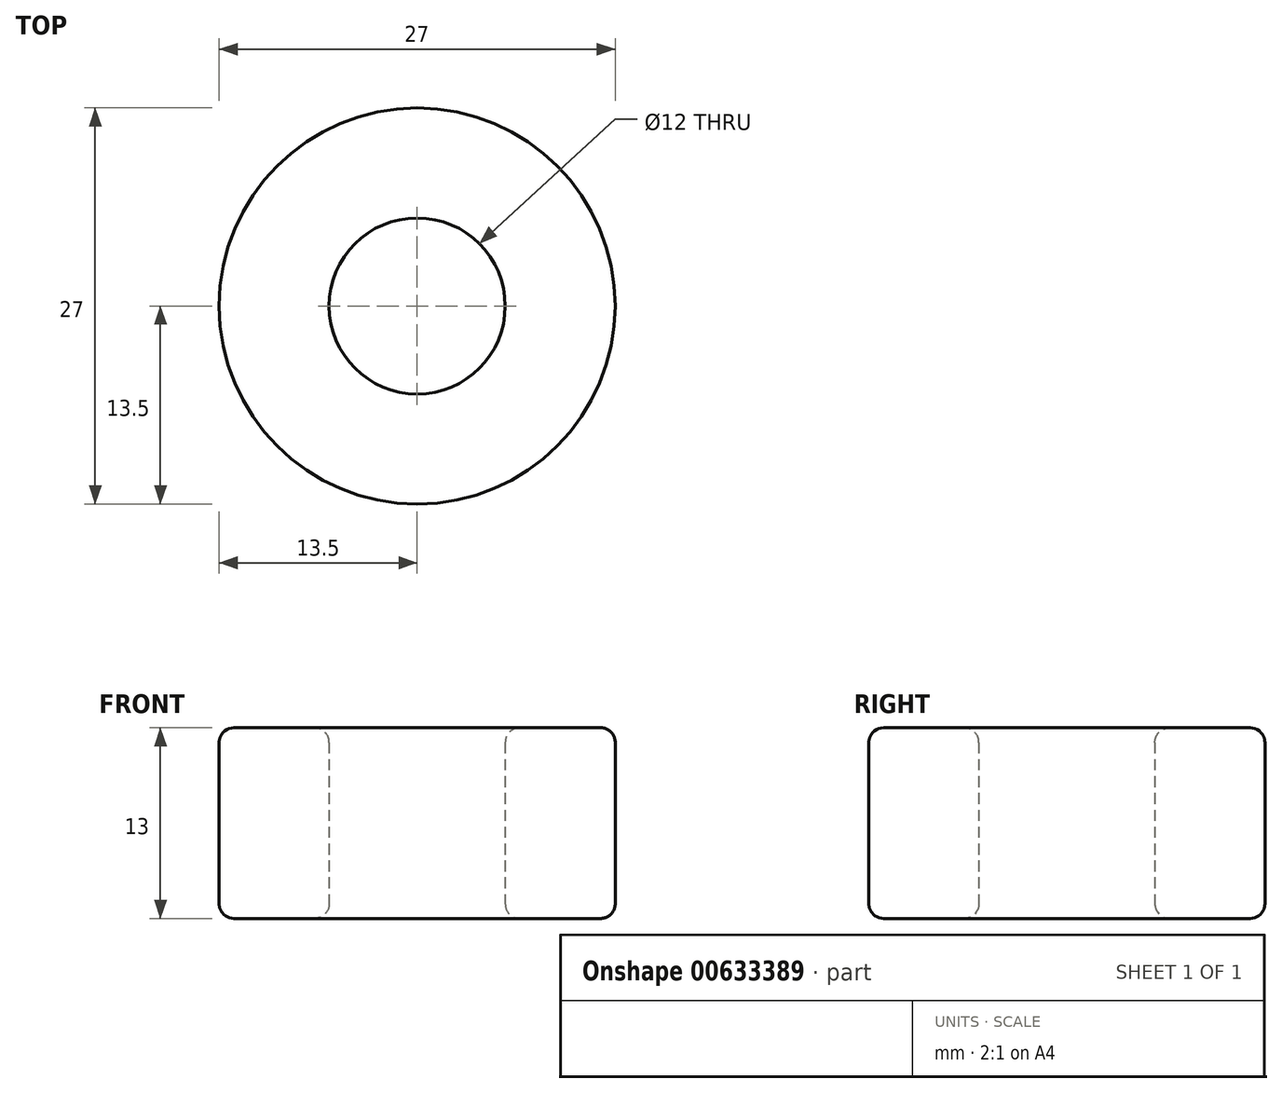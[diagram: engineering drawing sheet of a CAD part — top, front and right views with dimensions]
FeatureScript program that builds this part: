
annotation { "Feature Type Name" : "Feature", "Feature Type Description" : "" }
export const myFeature = defineFeature(function(context is Context, id is Id, definition is map)
    precondition{}
    {
        {
            var Q0;
            Q0=qCreatedBy(makeId("Top.planeOp"),FACE);
            var sketch = newSketch(context, id + "F0", { "sketchPlane" : qUnion([Q0])});
            skCircle(sketch, "E0", {"center": v(0, 0) * mm, "radius": 13.5 * mm});
            skCircle(sketch, "E1", {"center": v(0, 0) * mm, "radius": 6 * mm});
            skSolve(sketch);
        }
        {
            var Q0;
            Q0 = qSketchRegion(id + "F0", true);
            extrude(context, id + "F1", {"entities" : qUnion([Q0]), "depth" : 13 * mm, "offsetDistance" : 25 * mm});
        }
        {
            var Q0;
            Q0=makeQuery(id+"F1.opExtrude","CAP_FACE",FACE,{"disambiguationData":[OSD([sQuery(id+"F0.wireOp",EDGE,"E0"),sQuery(id+"F0.wireOp",EDGE,"E1")])],"isStart":false});
            var Q1;
            Q1=makeQuery(id+"F1.opExtrude","CAP_FACE",FACE,{"disambiguationData":[OSD([sQuery(id+"F0.wireOp",EDGE,"E0"),sQuery(id+"F0.wireOp",EDGE,"E1")])],"isStart":true});
            fillet(context, id + "F2", {"entities" : qUnion([Q0, Q1]), "radius" : 1 * mm, "tangentPropagation" : true, "allowEdgeOverflow" : false});
        }
    });
